# Revit family: TR3013
name_source: partatom
category: Verbindungsmittel
units: mm (PartAtom-declared; Revit-internal decimal feet)

## family parameters
Arbeitsebenenbasiert = Nein
Beim Laden mit Abzugskörper schneiden = Nein
Gemeinsam genutzt = Nein
Immer vertikal = Nein
OmniClass-Nummer = 23.25.10.27.11.21
OmniClass-Titel = Reinforcement Couplers

## types (10) — shared parameters
Endenbearbeitung 1 = Mit Gewinde
Endenbearbeitung 2 = Mit Gewinde
Hersteller = Stahlwerk Annahütte Max Aicher GmbH Co.KG
Körper = 0,00 kg
Modell = TR 3013
TR3013-L_Vis = Ja
TR3013-SW_Vis = Ja
Typenbild = TR3013.png
URL = http//:www.annahuette.com

## per-type parameters (varying)
| type | Außendurchmesser | Beschreibung | Einfassung Stab 1 | Einfassung Stab 2 | Gesamtlänge | Stabgröße 1 | Stabgröße 2 | TR3013-L | TR3013-Lm | TR3013-Lw | TR3013-SW | TR3013-ø | TR3013-ød | Typenkommentare |
| TR 3013-ø18 | 41 mm  [stored 0.134514 ft] | TR3013-ø18 | 23 mm  [stored 0.0754593 ft] | 23 mm  [stored 0.0754593 ft] | 60 mm  [stored 0.19685 ft] | SAS 670 - ø18 | SAS 670 - ø18 | 15 mm  [stored 0.0492126 ft] | 45 mm  [stored 0.147638 ft] | 60 mm  [stored 0.19685 ft] | 41 mm  [stored 0.134514 ft] | 23 mm  [stored 0.0754593 ft] | 18 mm  [stored 0.0590551 ft] | TR 3013 - Wechselstück |
| TR 3013-ø22 | 46 mm  [stored 0.150919 ft] | TR3013-ø22 | 25 mm  [stored 0.082021 ft] | 25 mm  [stored 0.082021 ft] | 65 mm  [stored 0.213255 ft] | SAS 670 - ø22 | SAS 670 - ø22 | 15 mm  [stored 0.0492126 ft] | 50 mm  [stored 0.164042 ft] | 65 mm  [stored 0.213255 ft] | 46 mm  [stored 0.150919 ft] | 27 mm  [stored 0.0885827 ft] | 22 mm  [stored 0.0721785 ft] | TR 30103- Wechselstück |
| TR 3013-ø25 | 55 mm  [stored 0.180446 ft] | TR3013-ø25 | 28 mm  [stored 0.0918635 ft] | 28 mm  [stored 0.0918635 ft] | 70 mm  [stored 0.229659 ft] | SAS 670 - ø25 | SAS 670 - ø25 | 15 mm  [stored 0.0492126 ft] | 55 mm  [stored 0.180446 ft] | 70 mm  [stored 0.229659 ft] | 55 mm  [stored 0.180446 ft] | 30 mm  [stored 0.0984252 ft] | 25 mm  [stored 0.082021 ft] | TR 3013 - Wechselstück |
| TR 3013-ø28 | 60 mm  [stored 0.19685 ft] | TR3013-ø28 | 30 mm  [stored 0.0984252 ft] | 30 mm  [stored 0.0984252 ft] | 80 mm  [stored 0.262467 ft] | SAS 670 - ø28 | SAS 670 - ø28 | 20 mm  [stored 0.0656168 ft] | 60 mm  [stored 0.19685 ft] | 80 mm  [stored 0.262467 ft] | 60 mm  [stored 0.19685 ft] | 33 mm  [stored 0.108268 ft] | 28 mm  [stored 0.0918635 ft] | TR 3013 - Wechselstück |
| TR 3013-ø30 | 65 mm  [stored 0.213255 ft] | TR3013-ø30 | 35 mm  [stored 0.114829 ft] | 35 mm  [stored 0.114829 ft] | 95 mm | SAS 670 - ø30 | SAS 670 - ø30 | 25 mm  [stored 0.082021 ft] | 70 mm  [stored 0.229659 ft] | 95 mm | 65 mm  [stored 0.213255 ft] | 35 mm  [stored 0.114829 ft] | 30 mm  [stored 0.0984252 ft] | TR 3013 - Wechselstück |
| TR 3013-ø35 | 80 mm  [stored 0.262467 ft] | TR3013-ø35 | 38 mm | 38 mm | 100 mm  [stored 0.328084 ft] | SAS 670 - ø35 | SAS 670 - ø35 | 25 mm  [stored 0.082021 ft] | 75 mm | 100 mm  [stored 0.328084 ft] | 80 mm  [stored 0.262467 ft] | 40 mm  [stored 0.131234 ft] | 35 mm  [stored 0.114829 ft] | TR 3013 - Wechselstück |
| TR 3013-ø43 | 90 mm  [stored 0.295276 ft] | TR3013-ø43 | 45 mm  [stored 0.147638 ft] | 45 mm  [stored 0.147638 ft] | 115 mm  [stored 0.377297 ft] | SAS 670 - ø43 | Keine | 25 mm  [stored 0.082021 ft] | 90 mm  [stored 0.295276 ft] | 115 mm  [stored 0.377297 ft] | 90 mm  [stored 0.295276 ft] | 48 mm  [stored 0.15748 ft] | 43 mm  [stored 0.141076 ft] | TR 3013 - Wechselstück |
| TR 3013-ø50 | 100 mm  [stored 0.328084 ft] | TR3013-ø50 | 50 mm  [stored 0.164042 ft] | 50 mm  [stored 0.164042 ft] | 125 mm  [stored 0.410105 ft] | SAS 670 - ø50 | Keine | 25 mm  [stored 0.082021 ft] | 100 mm  [stored 0.328084 ft] | 125 mm  [stored 0.410105 ft] | 100 mm  [stored 0.328084 ft] | 55 mm  [stored 0.180446 ft] | 50 mm  [stored 0.164042 ft] | TR 3013 - Wechselstück |
| TR 3013-ø57,5 | 100 mm  [stored 0.328084 ft] | TR3013-ø57,5 | 50 mm  [stored 0.164042 ft] | 50 mm  [stored 0.164042 ft] | 135 mm  [stored 0.442913 ft] | SAS 670 - ø57,5 | Keine | 35 mm  [stored 0.114829 ft] | 100 mm  [stored 0.328084 ft] | 135 mm  [stored 0.442913 ft] | 100 mm  [stored 0.328084 ft] | 63 mm | 58 mm | TR 3013 - Wechselstück |
| TR 3013-ø63,5 | 100 mm  [stored 0.328084 ft] | TR3013-ø63,5 | 53 mm | 53 mm | 140 mm  [stored 0.459318 ft] | SAS 670 - ø63,5 | Keine | 35 mm  [stored 0.114829 ft] | 105 mm  [stored 0.344488 ft] | 140 mm  [stored 0.459318 ft] | 100 mm  [stored 0.328084 ft] | 69 mm | 64 mm | TR 3013 - Wechselstück |

note: [stored X ft] marks values corroborated as IEEE doubles in the binary element streams (Revit-internal decimal feet)
